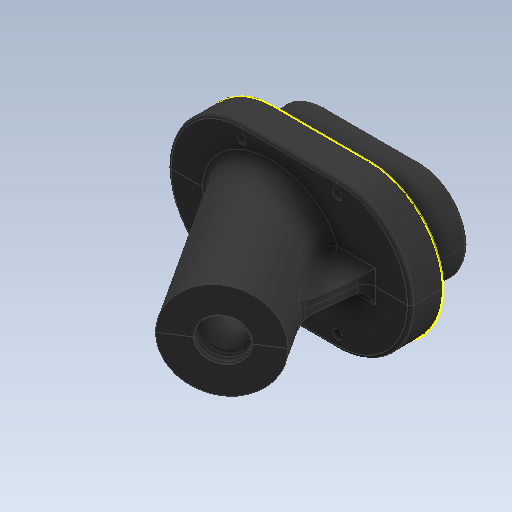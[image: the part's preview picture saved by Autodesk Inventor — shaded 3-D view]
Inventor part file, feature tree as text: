
AUTODESK INVENTOR PART (.ipt)
format: ipt  version: 2020 (Build 240168000, 168)  size: 876,032 bytes
history: native  units: mm
features: sketch x10, extrude x8, projected_geometry x5, other x5, fillet x4, reference x4, move_body x2, plane x1, split x1, direct_edit x1, hole x1, sweep x1
ambient origin geometry x8: Origin, YZ Plane, XZ Plane, XY Plane, X Axis, Y Axis, Z Axis, Center Point
bodies: Solid1 (feature_tree), Solid2 (feature_tree), Solid3 (feature_tree)
feature tree (43):
  sketch  "Sketch1"  dims[d0=16.0mm d1=0.0mm d2=10.0mm d3=0.0mm]
  extrude  "Extrusion1"  Depth=10.0mm TaperAngle=0.0deg
  extrude  "Extrusion2"  Depth=30.0mm
  plane  "Work Plane3"
  extrude  "Extrusion3"  Depth=20.0mm
  extrude  "Extrusion4"  Depth=1.0mm
  fillet  "Fillet1"  Radius=4.0mm
  split  "Split1"
  extrude  "Extrusion5"  Depth=0.1mm
  direct_edit  "Direct Edit1"
  extrude  "Extrusion6"  TaperAngle=0.0deg  [1 undecoded]
  extrude  "Extrusion7"  TaperAngle=0.0deg  [1 undecoded]
  extrude  "Extrusion8"  Depth=30.0mm TaperAngle=0.0deg
  hole  "Hole1"  [1 undecoded]
  sweep  "Sweep1"
  fillet  "Fillet2"  Radius=12.2mm
  fillet  "Fillet3"  Radius=0.5mm
  fillet  "Fillet4"  Radius=0.5mm
  reference  "Reference1"
  sketch  "Sketch4"  dims[d4=8.0mm d5=30.0mm]
  sketch  "Sketch5"  dims[d6=50.0mm d7=8.0mm d8=0.0mm d9=0.0mm d10=20.0mm]
  projected_geometry  "Projected Loop1"
  projected_geometry  "Projected Loop2"
  projected_geometry  "Projected Loop3"
  sketch  "Sketch6"  dims[d11=6.981317mm d12=1.0mm d13=4.0mm d14=0.0mm]
  reference  "Reference2"
  reference  "Reference3"
  reference  "Reference4"
  sketch  "Sketch7"  dims[d15=3.0mm d16=0.1mm]
  sketch  "Sketch8"  dims[d17=25.4mm d18=0.0mm d19=0.0mm d20=0.0mm d21=-8.25mm]
  sketch  "Sketch9"  dims[d22=10.0mm d23=0.0mm d24=0.0mm d25=0.0mm d26=-10.75mm]
  sketch  "Sketch10"  dims[d27=12.7mm d28=30.0mm d29=0.0mm]
  projected_geometry  "Projected Loop4"
  projected_geometry  "Projected Loop5"
  sketch  "Sketch11"  dims[d30=12.2mm d31=0.5mm d32=10.0mm d33=12.2mm d34=0.0mm d35=3.0mm d36=6.0mm d37=4.0mm d38=2.0mm d39=90.0deg d40=8.0mm d41=20.594885mm d42=0.5mm d43=0.5mm d44=0.5mm d45=0.5mm d46=0.5mm d47=0.1mm d48=1.0mm d49=0.5mm d50=1.5mm d51=40.0mm d52=12.7mm d53=0.0mm d54=0.0mm d55=0.0mm d56=0.1mm d57=1.0mm d58=1.0mm]
  sketch  "3D Sketch1"
  other  "Helical Curve1"
  other  "<userpath>\Documents\GitHub\OpenRaman\Hardware\OpenRaman.V1.iam"
  other  "OpenRaman.V1.iam"
  other  "SpectometerTube:1"
  other  "PrismsGeometry:1"
  move_body  "Move1"
  move_body  "Move2"
note: 3 required parameter values undecoded (feature->parameter linkage not recoverable at this tier; creation-order binding heuristic only, values carry confidence <= 0.55)
